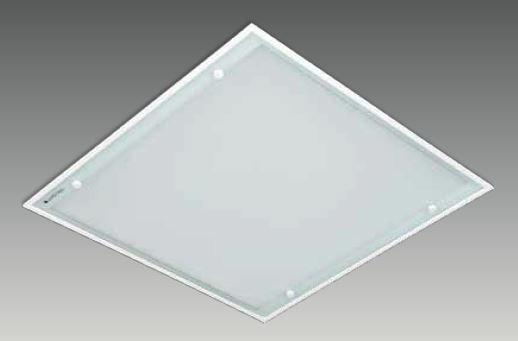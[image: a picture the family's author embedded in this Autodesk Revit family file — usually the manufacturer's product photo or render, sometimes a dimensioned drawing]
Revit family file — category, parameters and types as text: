
# Revit family: E 6060 GAC
name_source: partatom
category: Lighting Fixtures
revit_build: Autodesk Revit 2017 (Build: 20160225_1515(x64)
units: mm (PartAtom-declared; Revit-internal decimal feet)

## family parameters
Always vertical = Yes
Cut with Voids When Loaded = No
Host = Ceiling
Light Source = Yes
OmniClass Number = 23.80.70.11
OmniClass Title = Luminaries for Internal Lighting
Part Type = Normal
Room Calculation Point = No
Round Connector Dimension = Use Diameter
Shared = No

## types (8) — shared parameters
Color Filter = 16777215
Dimming Lamp Color Temperature Shift = <None>
Emit Shape Visible in Rendering = Yes
Emit from Rectangle Length = 510 mm  [stored 1.67323 ft]
Emit from Rectangle Width = 510 mm  [stored 1.67323 ft]
Light Source Symbol Size = 610 mm
Manufacturer = ARLIGHT
Type Image = E 6060 GAC.JPG

## per-type parameters (varying)
| type | Apparent Load | Wattage Comments |
| EGAC.6060.36.30.90 | 36 VA | 36 |
| EGAC.6060.28.30.80 | 28 VA | 28 |
| EGAC.6060.28.40.80 | 28 VA | 28 |
| EGAC.6060.36.30.80 | 36 VA | 36 |
| EGAC.6060.36.40.80 | 36 VA | 36 |
| EGAC.6060.28.30.90 | 28 VA | 28 |
| EGAC.6060.28.40.90 | 28 VA | 28 |
| EGAC.6060.36.40.90 | 36 VA | 36 |

note: [stored X ft] marks values corroborated as IEEE doubles in the binary element streams (Revit-internal decimal feet)

## geometry (parser evidence)
native form markers: Sweep x2
no freeform markers — native parametric forms only
